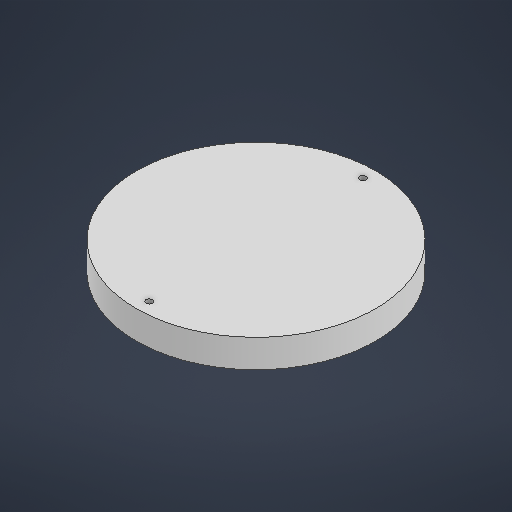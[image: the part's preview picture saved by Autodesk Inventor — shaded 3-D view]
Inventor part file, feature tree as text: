
AUTODESK INVENTOR PART (.ipt)
format: ipt  version: 2025 (Build 290162000, 162)  size: 183,808 bytes
history: native  units: in
note: dims shown in document units (in); Inventor stores cm internally (conversion verified against a paired STEP export)
features: extrude x2, sketch x2
ambient origin geometry x8: Origin, YZ Plane, XZ Plane, XY Plane, X Axis, Y Axis, Z Axis, Center Point
bodies: Solid1 (feature_tree)
feature tree (4):
  extrude  "Extrusion1"  Depth=0.7874in TaperAngle=0.0deg
  extrude  "Extrusion2"  Depth=0.7874in
  sketch  "Sketch1"  dims[d0=6.6929in d1=0.7874in d2=0.0in]
  sketch  "Sketch2"  dims[d3=5.9843in d4=0.1772in d5=0.1772in d6=0.7874in d7=0.0in]
